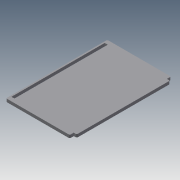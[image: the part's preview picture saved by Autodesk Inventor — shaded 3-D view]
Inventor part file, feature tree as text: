
AUTODESK INVENTOR PART (.ipt)
format: ipt  version: 2014 (Build 180170000, 170)  size: 103,936 bytes
history: native  units: mm
features: extrude x2, sketch x2, fillet x1
ambient origin geometry x8: Origin, YZ Plane, XZ Plane, XY Plane, X Axis, Y Axis, Z Axis, Center Point
bodies: Solid1 (feature_tree)
feature tree (5):
  extrude  "Extrusion1"  Depth=128.0mm
  extrude  "Extrusion2"  Depth=6.25mm
  fillet  "Fillet1"  Radius=2.875mm
  sketch  "Sketch1"  dims[d0=128.0mm d1=85.0mm]
  sketch  "Sketch2"  dims[d2=185.0mm d3=6.25mm d4=2.875mm d5=8.0mm d6=8.0mm d7=6.0mm d8=0.0mm d9=8.1mm d10=8.1mm d11=6.0mm d12=6.0mm d13=0.0mm d14=2.0mm]
